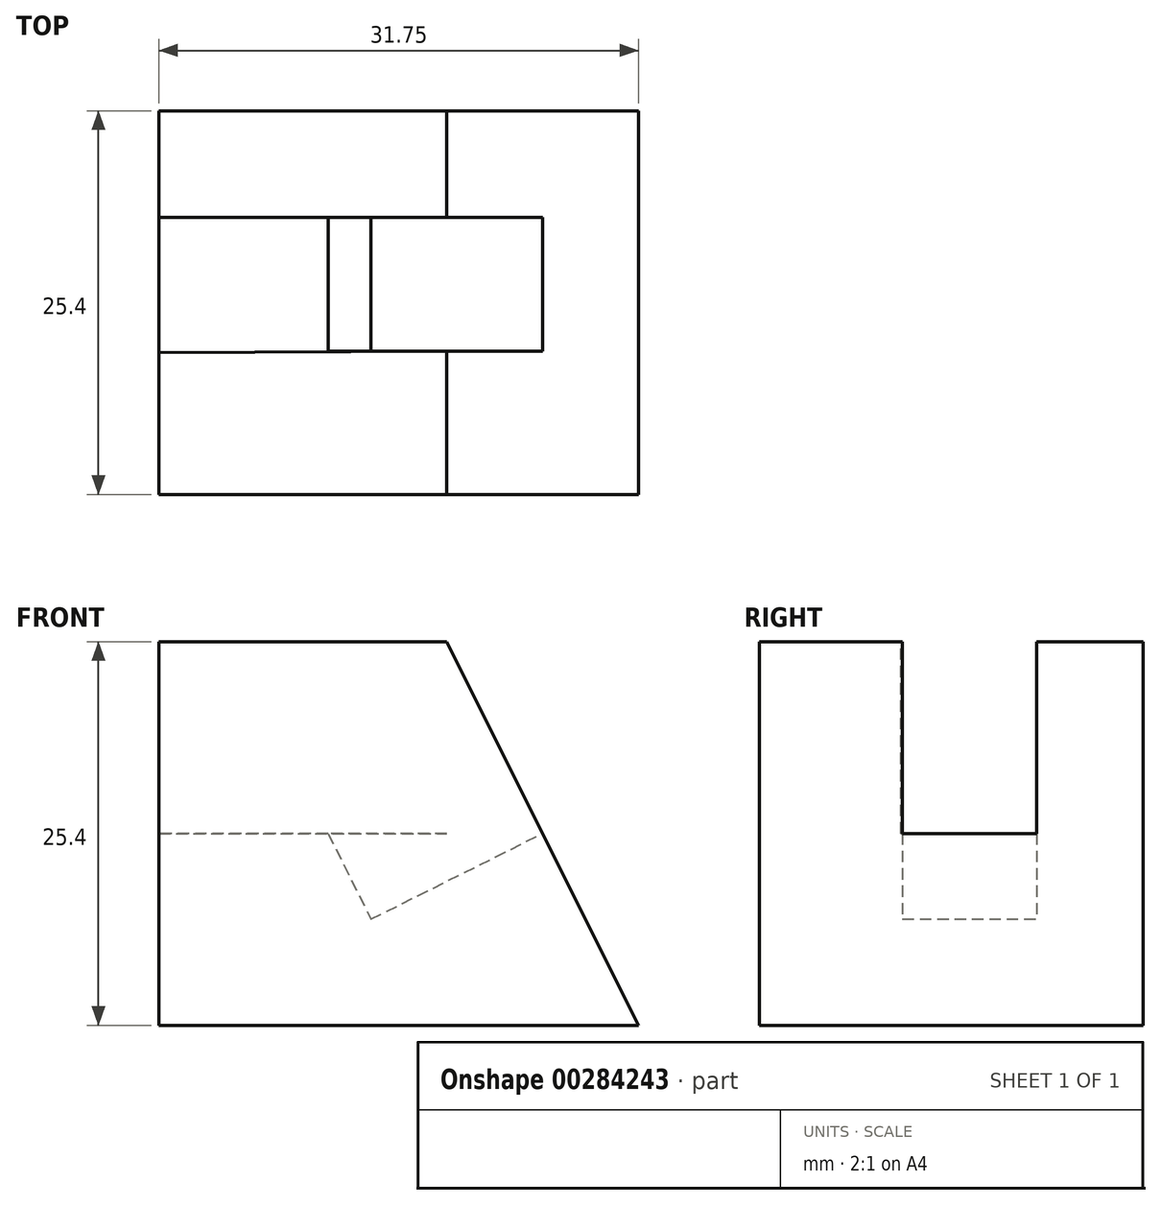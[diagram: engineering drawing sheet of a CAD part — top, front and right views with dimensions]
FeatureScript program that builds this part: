
annotation { "Feature Type Name" : "Feature", "Feature Type Description" : "" }
export const myFeature = defineFeature(function(context is Context, id is Id, definition is map)
    precondition{}
    {
        {
            var Q0;
            Q0=qCreatedBy(makeId("Front.planeOp"),FACE);
            var sketch = newSketch(context, id + "F0", { "sketchPlane" : qUnion([Q0])});
            skLineSegment(sketch, "E0", {"start": v(0, 0) * mm, "end": v(31.75, 0) * mm});
            skLineSegment(sketch, "E1", {"start": v(31.75, 0) * mm, "end": v(19.05, 25.4) * mm});
            skLineSegment(sketch, "E2", {"start": v(19.05, 25.4) * mm, "end": v(0, 25.4) * mm});
            skLineSegment(sketch, "E3", {"start": v(0, 25.4) * mm, "end": v(0, 0) * mm});
            skSolve(sketch);
        }
        {
            var Q0;
            Q0 = qSketchRegion(id + "F0", true);
            extrude(context, id + "F1", {"entities" : qUnion([Q0]), "depth" : 25.4 * mm});
        }
        {
            var Q0;
            Q0=makeQuery(id+"F1.opExtrude","SWEPT_FACE",FACE,{"disambiguationData":[OSD([sQuery(id+"F0.wireOp",EDGE,"E1")])]});
            var sketch = newSketch(context, id + "F2", { "sketchPlane" : qUnion([Q0])});
            skPoint(sketch, "E4.oppositeSnap0", {"position": v(-25.4, 0) * mm});
            skLineSegment(sketch, "E4.bottom", {"start": v(-15.92, 14.2) * mm, "end": v(-7.05, 14.2) * mm});
            skLineSegment(sketch, "E4.top", {"start": v(-15.92, 0) * mm, "end": v(-7.05, 0) * mm});
            skLineSegment(sketch, "E4.left", {"start": v(-15.92, 14.2) * mm, "end": v(-15.92, 0) * mm});
            skLineSegment(sketch, "E4.right", {"start": v(-7.05, 14.2) * mm, "end": v(-7.05, 0) * mm});
            skSolve(sketch);
        }
        {
            var Q0;
            Q0 = qSketchRegion(id + "F2", true);
            extrude(context, id + "F3", {"entities" : qUnion([Q0]), "operationType" : NewBodyOperationType.REMOVE, "endBound" : BoundingType.SYMMETRIC, "oppositeDirection" : true, "depth" : 25.4 * mm});
        }
        {
            var Q0;
            Q0=makeQuery(id+"F1.opExtrude","SWEPT_FACE",FACE,{"disambiguationData":[OSD([sQuery(id+"F0.wireOp",EDGE,"E2")])]});
            var sketch = newSketch(context, id + "F4", { "sketchPlane" : qUnion([Q0])});
            skLineSegment(sketch, "E5", {"start": v(19.05, -7.05) * mm, "end": v(0, -7.05) * mm});
            skLineSegment(sketch, "E6", {"start": v(0, -7.05) * mm, "end": v(0, -16.02) * mm});
            skLineSegment(sketch, "E7", {"start": v(0, -16.02) * mm, "end": v(19.05, -15.92) * mm});
            skSolve(sketch);
        }
        {
            var Q0;
            Q0 = qSketchRegion(id + "F4", true);
            var Q1;
            Q1=makeQuery(id+"F4.imprint","IMPRINT",FACE,{"disambiguationData":[TD([[makeQuery(id+"F4.imprint","IMPRINT",EDGE,{"derivedFrom":sQuery(id+"F4.wireOp",EDGE,"E5")}),1.0]])]});
            extrude(context, id + "F5", {"entities" : qUnion([Q0, Q1]), "operationType" : NewBodyOperationType.REMOVE, "endBound" : BoundingType.SYMMETRIC, "oppositeDirection" : true, "depth" : 25.4 * mm});
        }
    });
